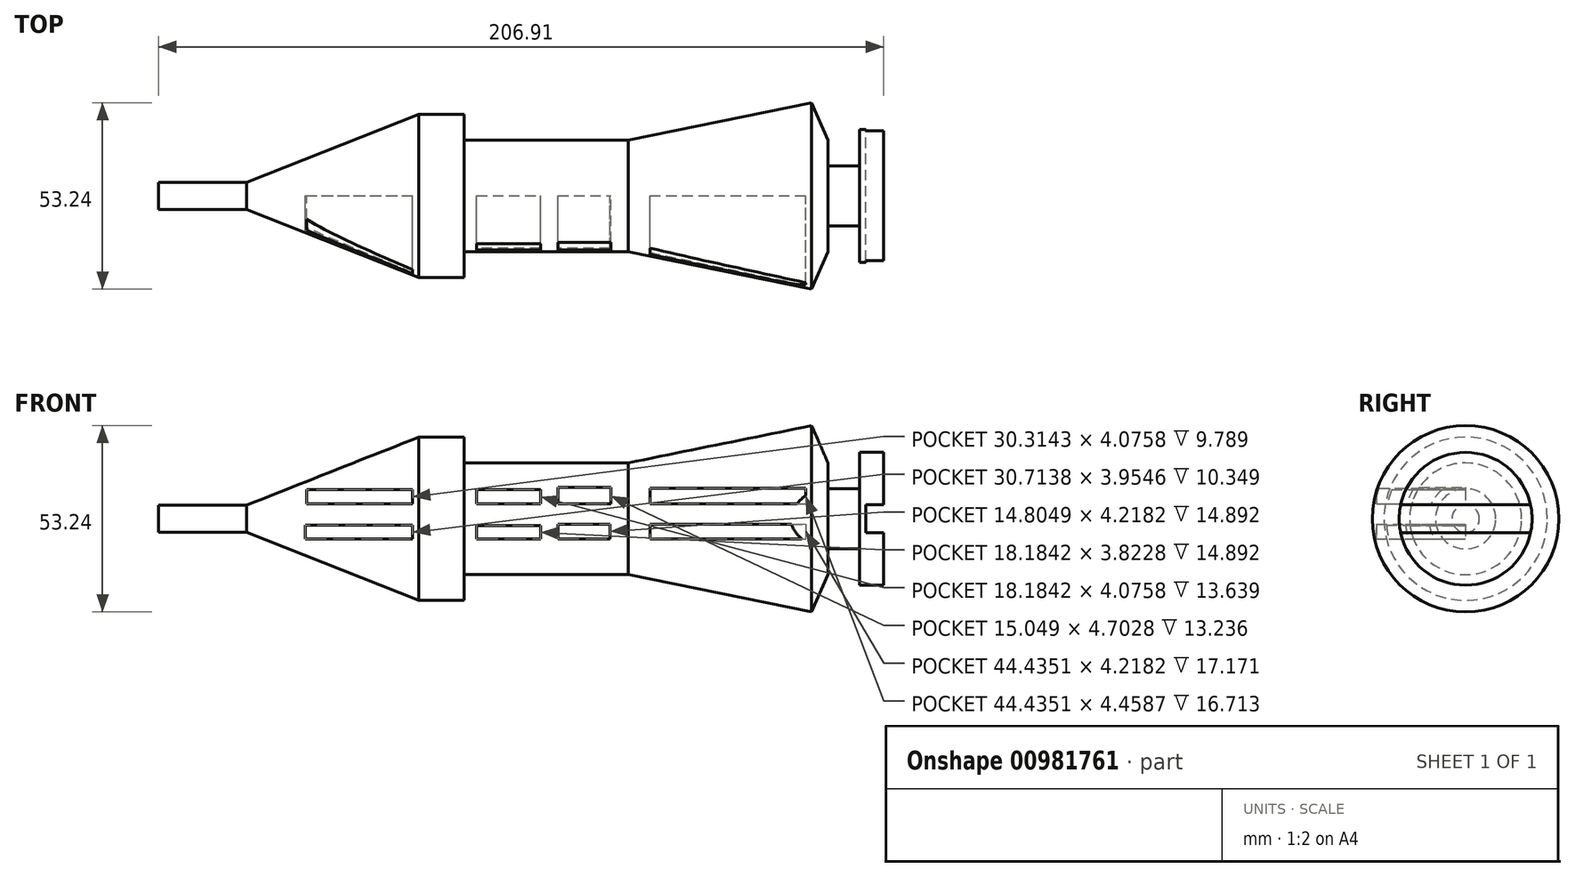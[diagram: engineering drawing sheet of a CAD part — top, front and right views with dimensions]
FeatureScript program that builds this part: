
annotation { "Feature Type Name" : "Feature", "Feature Type Description" : "" }
export const myFeature = defineFeature(function(context is Context, id is Id, definition is map)
    precondition{}
    {
        {
            var Q0;
            Q0=qCreatedBy(makeId("Front.planeOp"),FACE);
            var sketch = newSketch(context, id + "F0", { "sketchPlane" : qUnion([Q0])});
            skLineSegment(sketch, "E0", {"start": v(-94.32, 0) * mm, "end": v(102.5, 0) * mm, "construction": true});
            skLineSegment(sketch, "E1", {"start": v(-87.2, 3.9) * mm, "end": v(-62.06, 3.9) * mm});
            skLineSegment(sketch, "E2", {"start": v(-62.06, 3.9) * mm, "end": v(-12.97, 23.34) * mm});
            skLineSegment(sketch, "E3", {"start": v(-12.97, 23.34) * mm, "end": v(0, 23.34) * mm});
            skLineSegment(sketch, "E4", {"start": v(0, 23.34) * mm, "end": v(0, 15.97) * mm});
            skLineSegment(sketch, "E5", {"start": v(0, 15.97) * mm, "end": v(46.82, 15.97) * mm});
            skLineSegment(sketch, "E6", {"start": v(46.82, 15.97) * mm, "end": v(99.23, 26.62) * mm});
            skLineSegment(sketch, "E7", {"start": v(99.23, 26.62) * mm, "end": v(103.87, 15.97) * mm});
            skLineSegment(sketch, "E8", {"start": v(103.87, 15.97) * mm, "end": v(103.87, 8.6) * mm});
            skLineSegment(sketch, "E9", {"start": v(103.87, 8.6) * mm, "end": v(112.88, 8.6) * mm});
            skLineSegment(sketch, "E10", {"start": v(112.88, 8.6) * mm, "end": v(112.88, 18.97) * mm});
            skLineSegment(sketch, "E11", {"start": v(112.88, 18.97) * mm, "end": v(119.7, 18.97) * mm});
            skLineSegment(sketch, "E12", {"start": v(119.7, 18.97) * mm, "end": v(119.7, 0) * mm});
            skLineSegment(sketch, "E13", {"start": v(-87.2, 3.9) * mm, "end": v(-87.2, 0) * mm});
            skLineSegment(sketch, "E14", {"start": v(-94.32, 0) * mm, "end": v(123.57, 0) * mm, "construction": true});
            skLineSegment(sketch, "E15", {"start": v(-87.2, 0) * mm, "end": v(119.7, 0) * mm});
            skSolve(sketch);
        }
        {
            var Q0;
            Q0 = qSketchRegion(id + "F0", true);
            var Q1;
            Q1=sQuery(id+"F0.wireOp",EDGE,"E15");
            revolve(context, id + "F1", {"surfaceOperationType" : NewSurfaceOperationType.NEW, "entities" : qUnion([Q0]), "axis" : qUnion([Q1]), "revolveType" : RevolveType.FULL});
        }
        {
            var Q0;
            Q0=qCreatedBy(makeId("Front.planeOp"),FACE);
            var sketch = newSketch(context, id + "F2", { "sketchPlane" : qUnion([Q0])});
            skLineSegment(sketch, "E16.bottom", {"start": v(-45, 8.3) * mm, "end": v(-14.68, 8.3) * mm});
            skLineSegment(sketch, "E16.top", {"start": v(-45, 4.23) * mm, "end": v(-14.68, 4.23) * mm});
            skLineSegment(sketch, "E16.left", {"start": v(-45, 8.3) * mm, "end": v(-45, 4.23) * mm});
            skLineSegment(sketch, "E16.right", {"start": v(-14.68, 8.3) * mm, "end": v(-14.68, 4.23) * mm});
            skLineSegment(sketch, "E17.bottom", {"start": v(3.6, 8.3) * mm, "end": v(21.79, 8.3) * mm});
            skLineSegment(sketch, "E17.top", {"start": v(3.6, 4.23) * mm, "end": v(21.79, 4.23) * mm});
            skLineSegment(sketch, "E17.left", {"start": v(3.6, 8.3) * mm, "end": v(3.6, 4.23) * mm});
            skLineSegment(sketch, "E17.right", {"start": v(21.79, 8.3) * mm, "end": v(21.79, 4.23) * mm});
            skLineSegment(sketch, "E18.bottom", {"start": v(26.8, 8.94) * mm, "end": v(41.86, 8.94) * mm});
            skLineSegment(sketch, "E18.top", {"start": v(26.8, 4.23) * mm, "end": v(41.86, 4.23) * mm});
            skLineSegment(sketch, "E18.left", {"start": v(26.8, 8.94) * mm, "end": v(26.8, 4.23) * mm});
            skLineSegment(sketch, "E18.right", {"start": v(41.86, 8.94) * mm, "end": v(41.86, 4.23) * mm});
            skLineSegment(sketch, "E19.bottom", {"start": v(53.07, 8.7) * mm, "end": v(97.5, 8.7) * mm});
            skLineSegment(sketch, "E19.top", {"start": v(53.07, 4.23) * mm, "end": v(97.5, 4.23) * mm});
            skLineSegment(sketch, "E19.left", {"start": v(53.07, 8.7) * mm, "end": v(53.07, 4.23) * mm});
            skLineSegment(sketch, "E19.right", {"start": v(97.5, 8.7) * mm, "end": v(97.5, 4.23) * mm});
            skLineSegment(sketch, "E20.bottom", {"start": v(-45.39, -1.81) * mm, "end": v(-14.68, -1.81) * mm});
            skLineSegment(sketch, "E20.top", {"start": v(-45.39, -5.77) * mm, "end": v(-14.68, -5.77) * mm});
            skLineSegment(sketch, "E20.left", {"start": v(-45.39, -1.81) * mm, "end": v(-45.39, -5.77) * mm});
            skLineSegment(sketch, "E20.right", {"start": v(-14.68, -1.81) * mm, "end": v(-14.68, -5.77) * mm});
            skLineSegment(sketch, "E21.bottom", {"start": v(3.6, -1.95) * mm, "end": v(21.79, -1.95) * mm});
            skLineSegment(sketch, "E21.top", {"start": v(3.6, -5.77) * mm, "end": v(21.79, -5.77) * mm});
            skLineSegment(sketch, "E21.left", {"start": v(3.6, -1.95) * mm, "end": v(3.6, -5.77) * mm});
            skLineSegment(sketch, "E21.right", {"start": v(21.79, -1.95) * mm, "end": v(21.79, -5.77) * mm});
            skLineSegment(sketch, "E22.bottom", {"start": v(26.8, -1.55) * mm, "end": v(41.61, -1.55) * mm});
            skLineSegment(sketch, "E22.top", {"start": v(26.8, -5.77) * mm, "end": v(41.61, -5.77) * mm});
            skLineSegment(sketch, "E22.left", {"start": v(26.8, -1.55) * mm, "end": v(26.8, -5.77) * mm});
            skLineSegment(sketch, "E22.right", {"start": v(41.61, -1.55) * mm, "end": v(41.61, -5.77) * mm});
            skLineSegment(sketch, "E23.bottom", {"start": v(53.07, -1.55) * mm, "end": v(97.5, -1.55) * mm});
            skLineSegment(sketch, "E23.top", {"start": v(53.07, -5.77) * mm, "end": v(97.5, -5.77) * mm});
            skLineSegment(sketch, "E23.left", {"start": v(53.07, -1.55) * mm, "end": v(53.07, -5.77) * mm});
            skLineSegment(sketch, "E23.right", {"start": v(97.5, -1.55) * mm, "end": v(97.5, -5.77) * mm});
            skSolve(sketch);
        }
        {
            var Q0;
            Q0 = qSketchRegion(id + "F2", true);
            extrude(context, id + "F3", {"entities" : qUnion([Q0]), "operationType" : NewBodyOperationType.REMOVE, "depth" : 25.4 * mm, "offsetDistance" : 25.4 * mm});
        }
        {
            var Q0;
            Q0=makeQuery(id+"F1.opRevolve","SWEPT_FACE",FACE,{"disambiguationData":[OSD([sQuery(id+"F0.wireOp",EDGE,"E12")])]});
            var sketch = newSketch(context, id + "F4", { "sketchPlane" : qUnion([Q0])});
            skLineSegment(sketch, "E24.bottom", {"start": v(-20.76, -4.02) * mm, "end": v(20.76, -4.02) * mm});
            skLineSegment(sketch, "E24.top", {"start": v(-20.76, 4.02) * mm, "end": v(20.76, 4.02) * mm});
            skLineSegment(sketch, "E24.left", {"start": v(-20.76, -4.02) * mm, "end": v(-20.76, 4.02) * mm});
            skLineSegment(sketch, "E24.right", {"start": v(20.76, -4.02) * mm, "end": v(20.76, 4.02) * mm});
            skPoint(sketch, "E24.middle", {"position": v(0, 0) * mm});
            skSolve(sketch);
        }
        {
            var Q0;
            Q0 = qSketchRegion(id + "F4", true);
            extrude(context, id + "F5", {"entities" : qUnion([Q0]), "operationType" : NewBodyOperationType.REMOVE, "oppositeDirection" : true, "depth" : 5.08 * mm, "offsetDistance" : 25.4 * mm});
        }
    });
